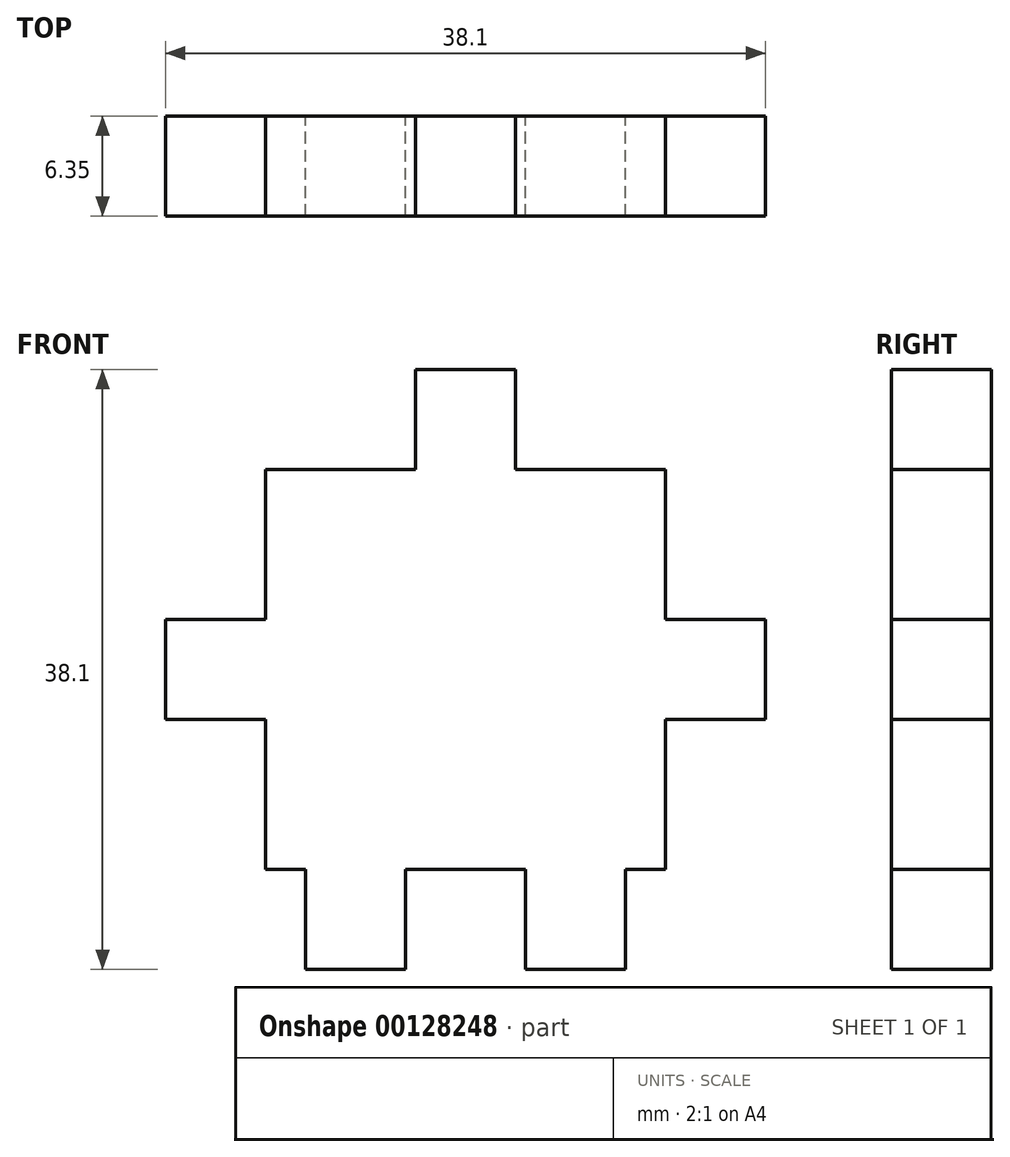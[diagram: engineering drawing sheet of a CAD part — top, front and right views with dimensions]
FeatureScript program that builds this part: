
annotation { "Feature Type Name" : "Feature", "Feature Type Description" : "" }
export const myFeature = defineFeature(function(context is Context, id is Id, definition is map)
    precondition{}
    {
        {
            var Q0;
            Q0=qCreatedBy(makeId("Front.planeOp"),FACE);
            var sketch = newSketch(context, id + "F0", { "sketchPlane" : qUnion([Q0])});
            skLineSegment(sketch, "E0.bottom", {"start": v(-44.11, 38.3) * mm, "end": v(-18.71, 38.3) * mm});
            skLineSegment(sketch, "E0.top", {"start": v(-44.11, 12.9) * mm, "end": v(-18.71, 12.9) * mm});
            skLineSegment(sketch, "E0.left", {"start": v(-44.11, 38.3) * mm, "end": v(-44.11, 12.9) * mm});
            skLineSegment(sketch, "E0.right", {"start": v(-18.71, 38.3) * mm, "end": v(-18.71, 12.9) * mm});
            skLineSegment(sketch, "E1.bottom", {"start": v(-41.57, 12.9) * mm, "end": v(-35.22, 12.9) * mm});
            skLineSegment(sketch, "E1.top", {"start": v(-41.57, 6.56) * mm, "end": v(-35.22, 6.56) * mm});
            skLineSegment(sketch, "E1.left", {"start": v(-41.57, 12.9) * mm, "end": v(-41.57, 6.56) * mm});
            skLineSegment(sketch, "E1.right", {"start": v(-35.22, 12.9) * mm, "end": v(-35.22, 6.56) * mm});
            skLineSegment(sketch, "E2.bottom", {"start": v(-21.25, 12.9) * mm, "end": v(-27.6, 12.9) * mm});
            skLineSegment(sketch, "E2.top", {"start": v(-21.25, 6.56) * mm, "end": v(-27.6, 6.56) * mm});
            skLineSegment(sketch, "E2.left", {"start": v(-21.25, 12.9) * mm, "end": v(-21.25, 6.56) * mm});
            skLineSegment(sketch, "E2.right", {"start": v(-27.6, 12.9) * mm, "end": v(-27.6, 6.56) * mm});
            skLineSegment(sketch, "E3.bottom", {"start": v(-44.11, 28.78) * mm, "end": v(-50.46, 28.78) * mm});
            skLineSegment(sketch, "E3.top", {"start": v(-44.11, 22.43) * mm, "end": v(-50.46, 22.43) * mm});
            skLineSegment(sketch, "E3.left", {"start": v(-44.11, 28.78) * mm, "end": v(-44.11, 22.43) * mm});
            skLineSegment(sketch, "E3.right", {"start": v(-50.46, 28.78) * mm, "end": v(-50.46, 22.43) * mm});
            skLineSegment(sketch, "E4.bottom", {"start": v(-18.71, 28.78) * mm, "end": v(-12.36, 28.78) * mm});
            skLineSegment(sketch, "E4.top", {"start": v(-18.71, 22.43) * mm, "end": v(-12.36, 22.43) * mm});
            skLineSegment(sketch, "E4.left", {"start": v(-18.71, 28.78) * mm, "end": v(-18.71, 22.43) * mm});
            skLineSegment(sketch, "E4.right", {"start": v(-12.36, 28.78) * mm, "end": v(-12.36, 22.43) * mm});
            skLineSegment(sketch, "E5.bottom", {"start": v(-34.59, 38.3) * mm, "end": v(-28.24, 38.3) * mm});
            skLineSegment(sketch, "E5.top", {"start": v(-34.59, 44.66) * mm, "end": v(-28.24, 44.66) * mm});
            skLineSegment(sketch, "E5.left", {"start": v(-34.59, 38.3) * mm, "end": v(-34.59, 44.66) * mm});
            skLineSegment(sketch, "E5.right", {"start": v(-28.24, 38.3) * mm, "end": v(-28.24, 44.66) * mm});
            skSolve(sketch);
        }
        {
            var Q0;
            Q0 = qSketchRegion(id + "F0", true);
            extrude(context, id + "F1", {"entities" : qUnion([Q0]), "depth" : 6.35 * mm});
        }
    });
